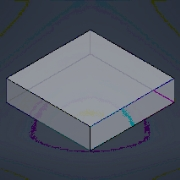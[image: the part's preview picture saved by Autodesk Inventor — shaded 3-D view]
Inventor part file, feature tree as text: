
AUTODESK INVENTOR PART (.ipt)
format: ipt  version: 2024.3 (Build 283343000, 343)  size: 135,680 bytes
history: native  units: mm
features: extrude x1, sketch x1
ambient origin geometry x8: Origin, YZ Plane, XZ Plane, XY Plane, X Axis, Y Axis, Z Axis, Center Point
bodies: Solid1 (feature_tree)
feature tree (2):
  extrude  "Extrusion1"  Depth=80.0mm
  sketch  "Sketch1"  dims[d0=80.0mm d1=80.0mm d2=40.0mm d3=0.0mm]
